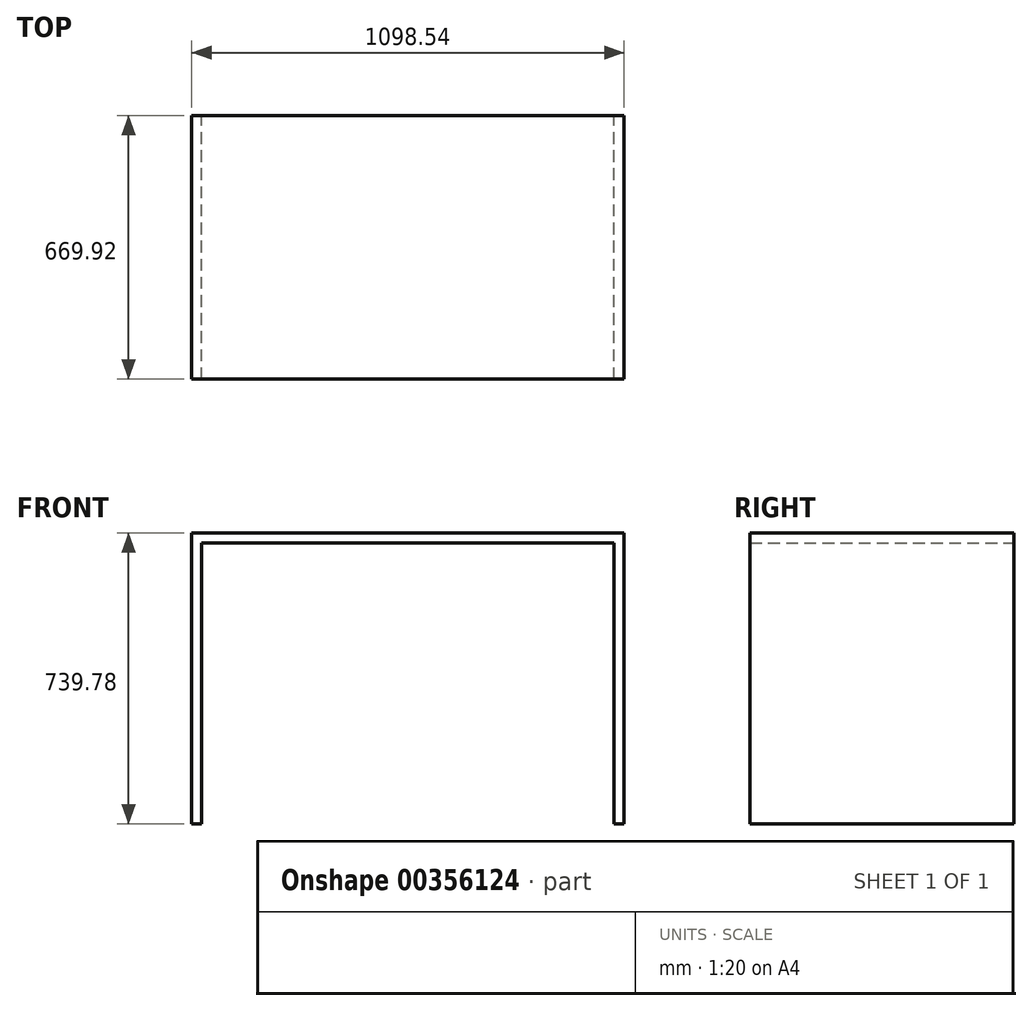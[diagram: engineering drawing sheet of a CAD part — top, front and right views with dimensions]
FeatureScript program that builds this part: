
annotation { "Feature Type Name" : "Feature", "Feature Type Description" : "" }
export const myFeature = defineFeature(function(context is Context, id is Id, definition is map)
    precondition{}
    {
        {
            var Q0;
            Q0=qCreatedBy(makeId("Front.planeOp"),FACE);
            var sketch = newSketch(context, id + "F0", { "sketchPlane" : qUnion([Q0])});
            skLineSegment(sketch, "E0.bottom", {"start": v(-549.27, 369.89) * mm, "end": v(549.28, 369.89) * mm});
            skLineSegment(sketch, "E0.top", {"start": v(-549.28, -369.89) * mm, "end": v(-523.88, -369.89) * mm});
            skLineSegment(sketch, "E0.left", {"start": v(-549.28, 369.89) * mm, "end": v(-549.28, -369.89) * mm});
            skLineSegment(sketch, "E0.right", {"start": v(549.28, 369.89) * mm, "end": v(549.27, -369.89) * mm});
            skPoint(sketch, "E0.middle", {"position": v(0, 0) * mm});
            skLineSegment(sketch, "E1.0", {"start": v(523.88, 344.49) * mm, "end": v(523.87, -369.89) * mm});
            skLineSegment(sketch, "E1.1", {"start": v(-523.88, 344.49) * mm, "end": v(523.88, 344.49) * mm});
            skLineSegment(sketch, "E1.2", {"start": v(-523.88, 344.49) * mm, "end": v(-523.88, -369.89) * mm});
            skLineSegment(sketch, "E2.trimOffspring", {"start": v(523.87, -369.89) * mm, "end": v(549.27, -369.89) * mm});
            skSolve(sketch);
        }
        {
            var Q0;
            Q0=makeQuery(id+"F0.imprint","IMPRINT",FACE,{"disambiguationData":[TD([[makeQuery(id+"F0.imprint","IMPRINT",EDGE,{"derivedFrom":sQuery(id+"F0.wireOp",EDGE,"E0.bottom")}),-1.0]])]});
            extrude(context, id + "F1", {"entities" : qUnion([Q0]), "endBound" : BoundingType.SYMMETRIC, "depth" : 669.92 * mm});
        }
    });
